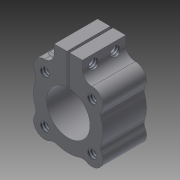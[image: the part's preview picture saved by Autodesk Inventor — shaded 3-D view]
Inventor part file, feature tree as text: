
AUTODESK INVENTOR PART (.ipt)
format: ipt  version: 2015 (Build 190159000, 159)  size: 268,800 bytes
history: native  units: in
note: dims shown in document units (in); Inventor stores cm internally (conversion verified against a paired STEP export)
features: hole x35, sketch x18, thread x12, other x1, extrude x1, imported_body x1
ambient origin geometry x8: Origin, YZ Plane, XZ Plane, XY Plane, X Axis, Y Axis, Z Axis, Center Point
bodies: Solid1 (feature_tree)
feature tree (68):
  other  "User Library-545340.sat1"
  thread  "Thread1"  [1 undecoded]
  thread  "Thread2"  [1 undecoded]
  thread  "Thread3"  [1 undecoded]
  thread  "Thread4"  [1 undecoded]
  thread  "Thread5"  [1 undecoded]
  thread  "Thread6"  [1 undecoded]
  thread  "Thread7"  [1 undecoded]
  thread  "Thread8"  [1 undecoded]
  hole  "Hole1"  [1 undecoded]
  hole  "Hole4"  [1 undecoded]
  hole  "Hole6"  [1 undecoded]
  hole  "Hole8"  [1 undecoded]
  hole  "Hole10"  [1 undecoded]
  hole  "Hole12"  [1 undecoded]
  hole  "Hole14"  [1 undecoded]
  hole  "Hole16"  [1 undecoded]
  hole  "Hole18"  [1 undecoded]
  thread  "Thread9"  [1 undecoded]
  thread  "Thread10"  [1 undecoded]
  thread  "Thread11"  [1 undecoded]
  thread  "Thread12"  [1 undecoded]
  hole  "Hole20"  [1 undecoded]
  hole  "Hole22"  [1 undecoded]
  hole  "Hole24"  [1 undecoded]
  hole  "Hole26"  [1 undecoded]
  sketch  "Sketch16"  dims[d108=0.104in d109=0.2565in d110=0.375in d111=0.25in d112=0.5635in d113=0.3255in d114=120.0deg]
  extrude  "Extrusion1"  [1 undecoded]
  hole  "Hole27"  [1 undecoded]
  hole  "Hole29"  [1 undecoded]
  hole  "Hole31"  [1 undecoded]
  hole  "Hole33"  [1 undecoded]
  hole  "Hole35"  [1 undecoded]
  imported_body  "Base1"
  sketch  "Sketch3"  dims[d23=0.104in d24=0.339in d25=0.375in d26=0.25in d27=0.5635in d28=0.408in d29=120.0deg]
  hole  "Hole2"  [1 undecoded]
  sketch  "Sketch4"  dims[d30=0.104in d31=0.2706in d32=0.375in d33=0.25in d34=0.5635in d35=0.3396in d36=120.0deg]
  hole  "Hole3"  [1 undecoded]
  sketch  "Sketch5"  dims[d37=0.104in d38=0.339in d39=0.375in d40=0.25in d41=0.5635in d42=0.408in d43=120.0deg]
  hole  "Hole5"  [1 undecoded]
  sketch  "Sketch6"  dims[d44=0.104in d45=0.138in d46=0.375in d47=0.25in d48=0.5635in d49=0.207in d50=120.0deg]
  hole  "Hole7"  [1 undecoded]
  sketch  "Sketch7"  dims[d51=0.104in d52=0.339in d53=0.375in d54=0.25in d55=0.5635in d56=0.408in d57=120.0deg]
  hole  "Hole9"  [1 undecoded]
  sketch  "Sketch8"  dims[d58=0.104in d59=0.339in d60=0.375in d61=0.25in d62=0.5635in d63=0.408in d64=120.0deg]
  hole  "Hole11"  [1 undecoded]
  sketch  "Sketch9"  dims[d65=0.104in d66=0.339in d67=0.375in d68=0.25in d69=0.5635in d70=0.408in d71=120.0deg]
  hole  "Hole13"  [1 undecoded]
  sketch  "Sketch10"  dims[d72=0.104in d73=0.339in d74=0.375in d75=0.25in d76=0.5635in d77=0.408in d78=120.0deg]
  hole  "Hole15"  [1 undecoded]
  sketch  "Sketch11"  dims[d79=0.104in d80=0.339in d81=0.375in d82=0.25in d83=0.5635in d84=0.408in d85=120.0deg d86=1.0in d87=0.0in]
  hole  "Hole17"  [1 undecoded]
  sketch  "Sketch12"  dims[d88=1.0in d89=0.0in d90=1.0in d91=0.0in]
  hole  "Hole19"  [1 undecoded]
  sketch  "Sketch13"  dims[d92=1.0in d93=0.0in]
  hole  "Hole21"  [1 undecoded]
  sketch  "Sketch14"  dims[d94=0.104in d95=0.2565in d96=0.375in d97=0.25in d98=0.5635in d99=0.3255in d100=120.0deg]
  hole  "Hole23"  [1 undecoded]
  sketch  "Sketch15"  dims[d101=0.104in d102=0.2565in d103=0.375in d104=0.25in d105=0.5635in d106=0.3255in d107=120.0deg]
  hole  "Hole25"  [1 undecoded]
  sketch  "Sketch17"  dims[d115=0.104in d116=0.2565in d117=0.375in d118=0.25in d119=0.5635in d120=0.3255in d121=120.0deg d122=1.0in d123=0.0in]
  hole  "Hole28"  [1 undecoded]
  sketch  "Sketch18"  dims[d124=0.14in d125=0.75in d126=0.375in d127=0.25in d128=0.5635in d129=1.0in d130=0.0in]
  hole  "Hole30"  [1 undecoded]
  sketch  "Sketch19"  dims[d131=0.104in d132=0.2042in d133=0.375in d134=0.25in d135=0.5635in d136=0.2732in d137=120.0deg]
  hole  "Hole32"  [1 undecoded]
  sketch  "Sketch20"  dims[d138=0.104in d139=0.2042in d140=0.375in d141=0.25in d142=0.5635in d143=0.2732in d144=120.0deg d145=0.104in d146=0.2042in d147=0.375in d148=0.25in d149=0.5635in d150=0.2732in d151=120.0deg d152=0.104in d153=0.2042in d154=0.375in d155=0.25in d156=0.5635in d157=0.2732in d158=120.0deg]
  hole  "Hole34"  [1 undecoded]
note: 48 required parameter values undecoded (feature->parameter linkage not recoverable at this tier; creation-order binding heuristic only, values carry confidence <= 0.55)
